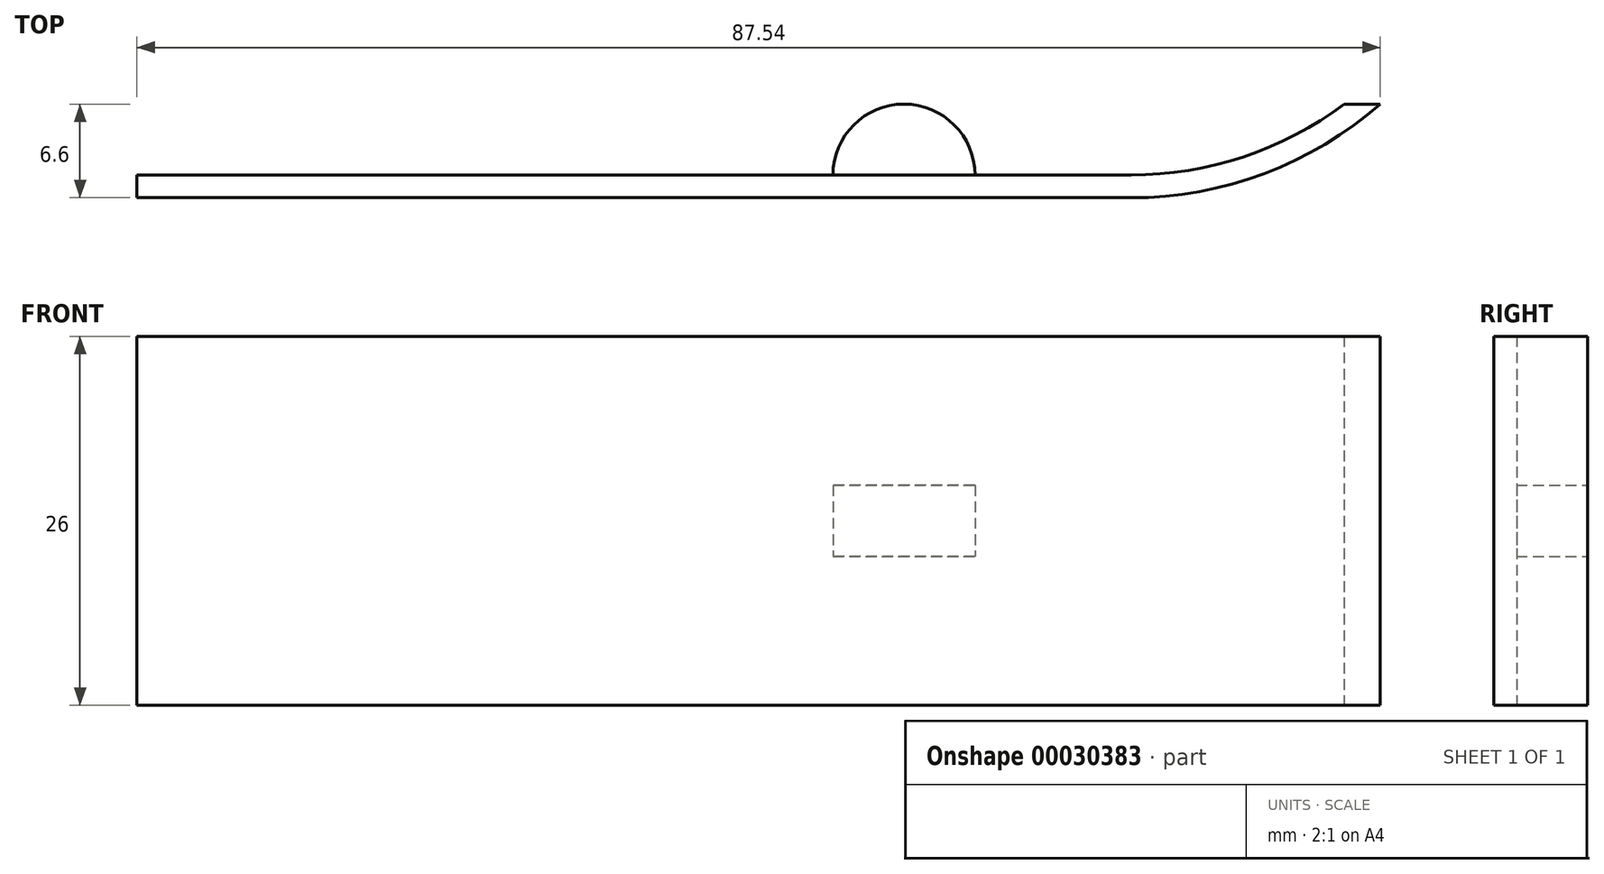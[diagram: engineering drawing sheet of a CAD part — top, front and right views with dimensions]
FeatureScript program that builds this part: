
annotation { "Feature Type Name" : "Feature", "Feature Type Description" : "" }
export const myFeature = defineFeature(function(context is Context, id is Id, definition is map)
    precondition{}
    {
        {
            var Q0;
            Q0=qCreatedBy(makeId("Top.planeOp"),FACE);
            var sketch = newSketch(context, id + "F0", { "sketchPlane" : qUnion([Q0])});
            skLineSegment(sketch, "E0.bottom", {"start": v(0, 0) * mm, "end": v(-70, 0) * mm});
            skLineSegment(sketch, "E0.top", {"start": v(0, 1.6) * mm, "end": v(-70, 1.6) * mm});
            skLineSegment(sketch, "E0.left", {"start": v(0, 0) * mm, "end": v(0, 1.6) * mm});
            skLineSegment(sketch, "E0.right", {"start": v(-70, 0) * mm, "end": v(-70, 1.6) * mm});
            skArc(sketch, "E1", {"start": v(0, 1.6) * mm, "mid": v(7.9, 2.88) * mm, "end": v(15, 6.6) * mm});
            skArc(sketch, "E2.0", {"start": v(0, 0) * mm, "mid": v(9.37, 1.7) * mm, "end": v(17.54, 6.6) * mm});
            skLineSegment(sketch, "E3", {"start": v(15, 6.6) * mm, "end": v(17.54, 6.6) * mm});
            skSolve(sketch);
        }
        {
            var Q0;
            Q0 = qSketchRegion(id + "F0", true);
            extrude(context, id + "F1", {"entities" : qUnion([Q0]), "depth" : 13 * mm, "hasSecondDirection" : true, "secondDirectionOppositeDirection" : true, "secondDirectionDepth" : 13 * mm});
        }
        {
            var Q0;
            Q0=makeQuery(id+"F1.opExtrude","SWEPT_FACE",FACE,{"disambiguationData":[OSD([sQuery(id+"F0.wireOp",EDGE,"E0.top")])]});
            var sketch = newSketch(context, id + "F2", { "sketchPlane" : qUnion([Q0])});
            skPoint(sketch, "E4", {"position": v(16, 0) * mm});
            skLineSegment(sketch, "E5.rect.bottom", {"start": v(16, 2.5) * mm, "end": v(21, 2.5) * mm});
            skLineSegment(sketch, "E5.rect.top", {"start": v(16, -2.5) * mm, "end": v(21, -2.5) * mm});
            skLineSegment(sketch, "E5.rect.right", {"start": v(21, 2.5) * mm, "end": v(21, -2.5) * mm});
            skLineSegment(sketch, "E6", {"start": v(16, 2.5) * mm, "end": v(16, -2.5) * mm});
            skPoint(sketch, "E5.rect.left.start.orphan", {"position": v(11, 2.5) * mm});
            skPoint(sketch, "E7.orphan", {"position": v(11, -2.5) * mm});
            skSolve(sketch);
        }
        {
            var Q0;
            Q0=makeQuery(id+"F2.imprint","IMPRINT",FACE,{"disambiguationData":[TD([[makeQuery(id+"F2.imprint","IMPRINT",EDGE,{"derivedFrom":sQuery(id+"F2.wireOp",EDGE,"E5.rect.bottom")}),-1.0]])]});
            var Q1;
            Q1=sQuery(id+"F2.wireOp",EDGE,"E6");
            revolve(context, id + "F3", {"operationType" : NewBodyOperationType.ADD, "entities" : qUnion([Q0]), "axis" : qUnion([Q1]), "revolveType" : RevolveType.ONE_DIRECTION, "angle" : 180 * degree});
        }
    });
